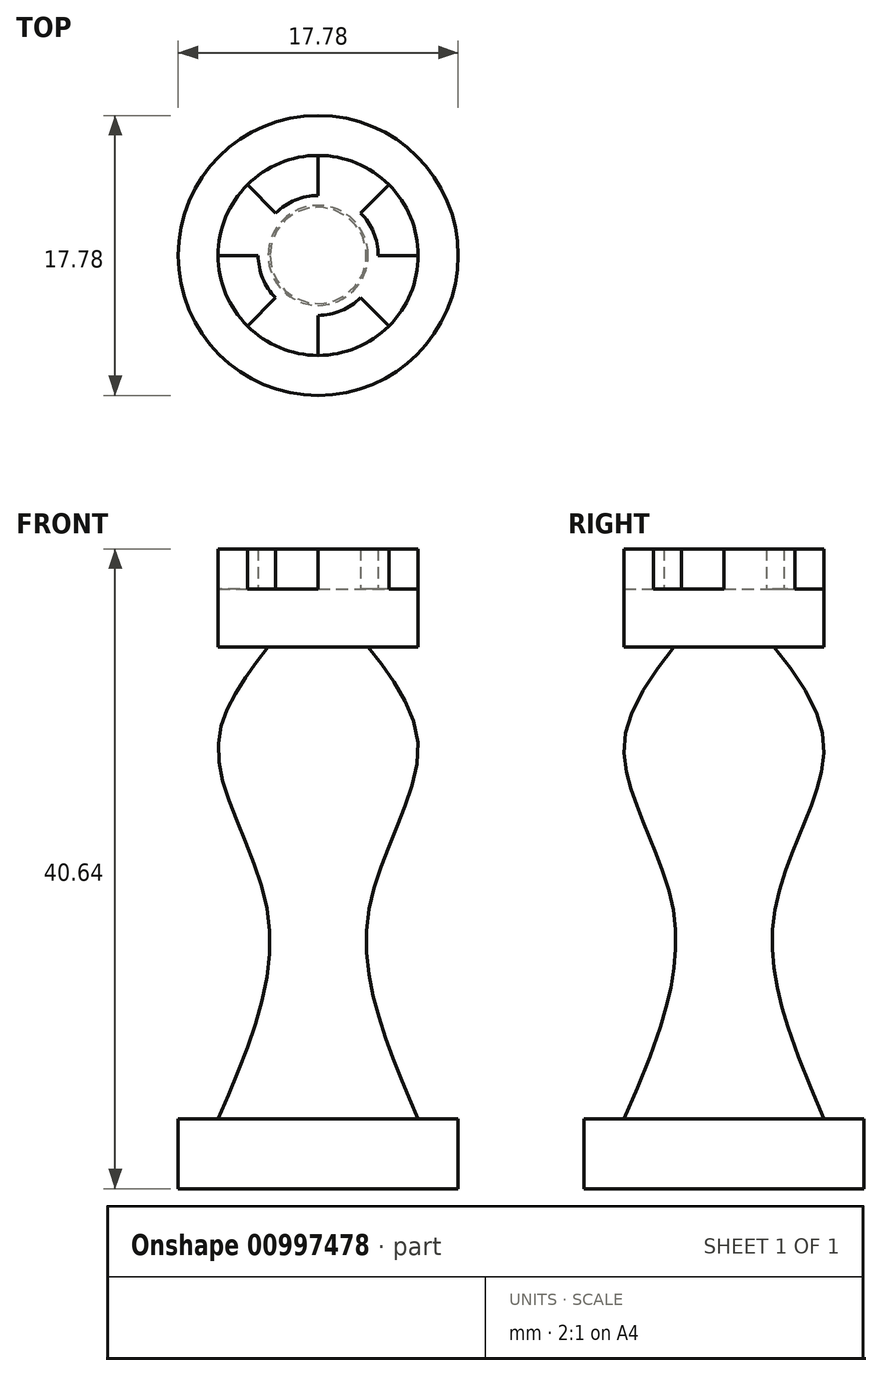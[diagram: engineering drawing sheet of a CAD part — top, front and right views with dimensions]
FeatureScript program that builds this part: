
annotation { "Feature Type Name" : "Feature", "Feature Type Description" : "" }
export const myFeature = defineFeature(function(context is Context, id is Id, definition is map)
    precondition{}
    {
        {
            var Q0;
            Q0=qCreatedBy(makeId("Front.planeOp"),FACE);
            var sketch = newSketch(context, id + "F0", { "sketchPlane" : qUnion([Q0])});
            skLineSegment(sketch, "E0", {"start": v(0, 0) * mm, "end": v(0, 38.1) * mm});
            skLineSegment(sketch, "E1", {"start": v(0, 0) * mm, "end": v(6.35, 0) * mm});
            skLineSegment(sketch, "E2.bottom", {"start": v(0, 38.1) * mm, "end": v(6.35, 38.1) * mm});
            skLineSegment(sketch, "E2.top", {"start": v(3.18, 34.42) * mm, "end": v(6.35, 34.42) * mm});
            skLineSegment(sketch, "E2.left", {"start": v(0, 38.1) * mm, "end": v(0, 34.42) * mm});
            skLineSegment(sketch, "E2.right", {"start": v(6.35, 38.1) * mm, "end": v(6.35, 34.42) * mm});
            skPoint(sketch, "E3.2.internal.snap0", {"position": v(3.18, 34.42) * mm});
            skFitSpline(sketch, "E3", {"points": [v(3.18, 34.42) * mm, v(6.35, 27.73) * mm, v(3.18, 17.35) * mm, v(6.35, 4.44) * mm], "startDerivative": vector(17.27, -22.35) * mm, "endDerivative": vector(14.98, -34.76) * mm});
            skLineSegment(sketch, "E4", {"start": v(6.35, 4.44) * mm, "end": v(8.9, 4.44) * mm});
            skLineSegment(sketch, "E5", {"start": v(8.9, 4.44) * mm, "end": v(8.9, 0) * mm});
            skLineSegment(sketch, "E6", {"start": v(8.9, 0) * mm, "end": v(6.35, 0) * mm});
            skSolve(sketch);
        }
        {
            var Q0;
            Q0 = qSketchRegion(id + "F0", true);
            var Q1;
            Q1=sQuery(id+"F0.wireOp",EDGE,"E0");
            revolve(context, id + "F1", {"surfaceOperationType" : NewSurfaceOperationType.NEW, "entities" : qUnion([Q0]), "axis" : qUnion([Q1]), "revolveType" : RevolveType.FULL});
        }
        {
            var Q0;
            Q0=makeQuery(id+"F1.opRevolve","SWEPT_FACE",FACE,{"disambiguationData":[OSD([sQuery(id+"F0.wireOp",EDGE,"E2.bottom")])]});
            var sketch = newSketch(context, id + "F2", { "sketchPlane" : qUnion([Q0])});
            skArc(sketch, "E7.0", {"start": v(0, 6.35) * mm, "mid": v(-2.43, 5.87) * mm, "end": v(-4.5, 4.5) * mm});
            skArc(sketch, "E8.0", {"start": v(0, 3.8) * mm, "mid": v(-1.46, 3.52) * mm, "end": v(-2.7, 2.7) * mm});
            skLineSegment(sketch, "E9", {"start": v(-6.35, 0) * mm, "end": v(6.35, 0) * mm, "construction": true});
            skArc(sketch, "E10.trimOffspring", {"start": v(6.35, 0) * mm, "mid": v(5.87, 2.43) * mm, "end": v(4.5, 4.5) * mm});
            skArc(sketch, "E11.trimOffspring", {"start": v(3.8, 0) * mm, "mid": v(3.52, 1.46) * mm, "end": v(2.7, 2.7) * mm});
            skArc(sketch, "E12.trimOffspring", {"start": v(0, -3.8) * mm, "mid": v(1.46, -3.52) * mm, "end": v(2.7, -2.7) * mm});
            skArc(sketch, "E13.trimOffspring", {"start": v(0, -6.35) * mm, "mid": v(2.43, -5.87) * mm, "end": v(4.5, -4.5) * mm});
            skArc(sketch, "E14.trimOffspring", {"start": v(-3.8, 0) * mm, "mid": v(-3.52, -1.46) * mm, "end": v(-2.7, -2.7) * mm});
            skArc(sketch, "E15.trimOffspring", {"start": v(-6.35, 0) * mm, "mid": v(-5.87, -2.43) * mm, "end": v(-4.5, -4.5) * mm});
            skLineSegment(sketch, "E16", {"start": v(-4.5, 4.5) * mm, "end": v(-2.7, 2.7) * mm});
            skLineSegment(sketch, "E17", {"start": v(0, 6.35) * mm, "end": v(0, 3.8) * mm});
            skLineSegment(sketch, "E18", {"start": v(2.7, 2.7) * mm, "end": v(4.5, 4.5) * mm});
            skLineSegment(sketch, "E19", {"start": v(6.35, 0) * mm, "end": v(3.8, 0) * mm});
            skLineSegment(sketch, "E20", {"start": v(4.5, -4.5) * mm, "end": v(2.7, -2.7) * mm});
            skLineSegment(sketch, "E21", {"start": v(0, -6.35) * mm, "end": v(0, -3.8) * mm});
            skLineSegment(sketch, "E22", {"start": v(-4.5, -4.5) * mm, "end": v(-2.7, -2.7) * mm});
            skLineSegment(sketch, "E23", {"start": v(-3.8, 0) * mm, "end": v(-6.35, 0) * mm});
            skSolve(sketch);
        }
        {
            var Q0;
            Q0 = qSketchRegion(id + "F2", true);
            extrude(context, id + "F3", {"entities" : qUnion([Q0]), "operationType" : NewBodyOperationType.ADD, "depth" : 2.54 * mm, "offsetDistance" : 25.4 * mm});
        }
    });
